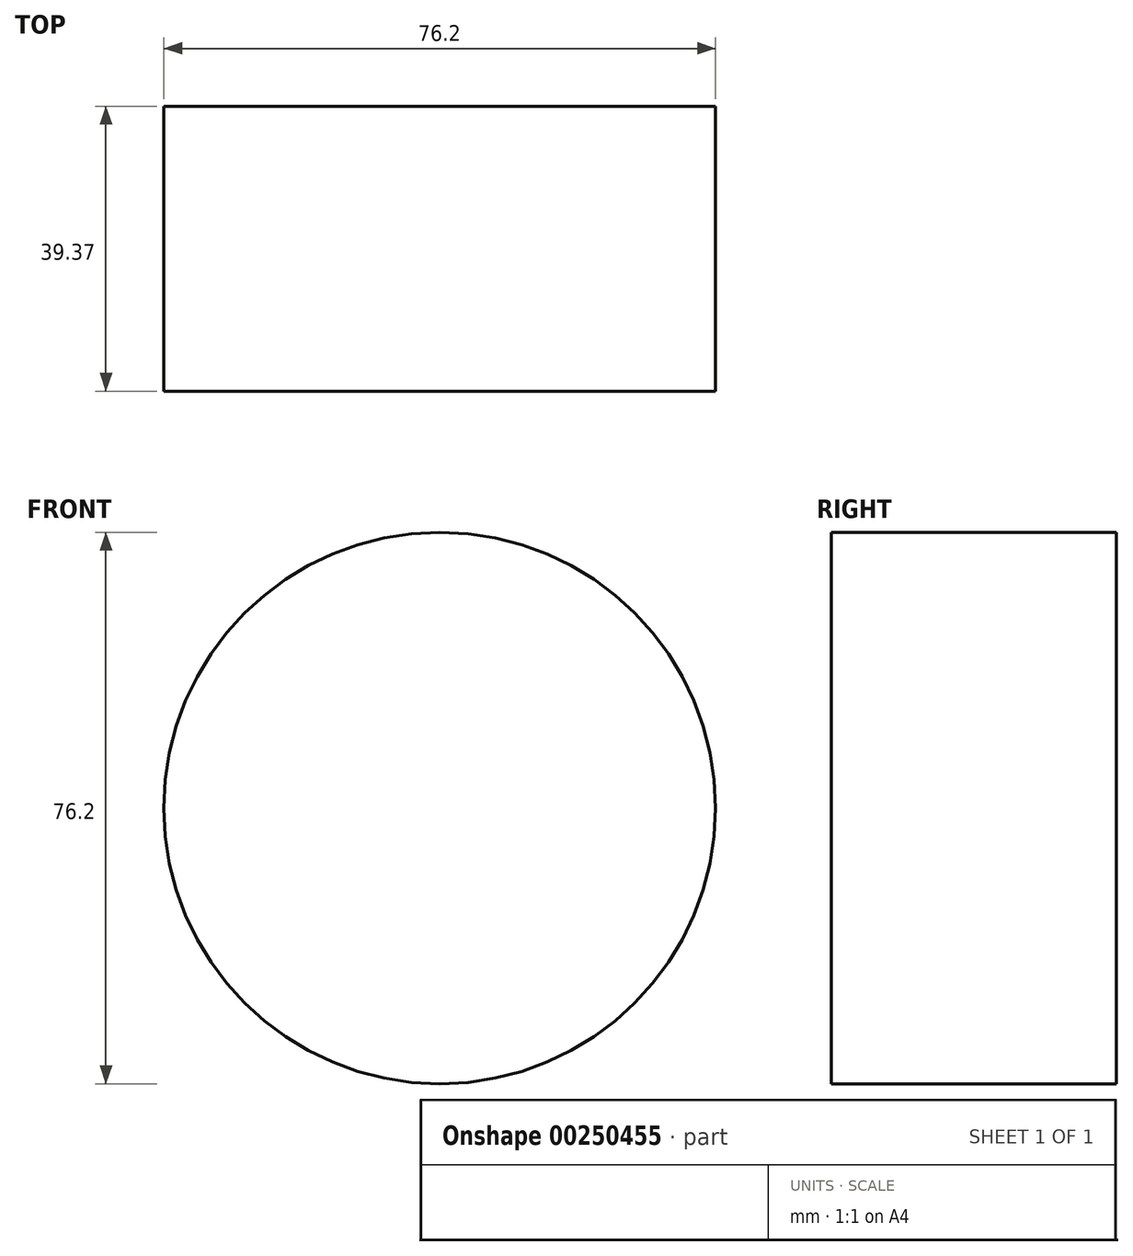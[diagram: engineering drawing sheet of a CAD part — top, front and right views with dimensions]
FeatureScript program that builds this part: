
annotation { "Feature Type Name" : "Feature", "Feature Type Description" : "" }
export const myFeature = defineFeature(function(context is Context, id is Id, definition is map)
    precondition{}
    {
        {
            var Q0;
            Q0=qCreatedBy(makeId("Front.planeOp"),FACE);
            var sketch = newSketch(context, id + "F0", { "sketchPlane" : qUnion([Q0])});
            skCircle(sketch, "E0", {"center": v(0, 0) * mm, "radius": 38.1 * mm});
            skSolve(sketch);
        }
        {
            var Q0;
            Q0 = qSketchRegion(id + "F0", true);
            extrude(context, id + "F1", {"entities" : qUnion([Q0]), "depth" : 39.37 * mm});
        }
    });
